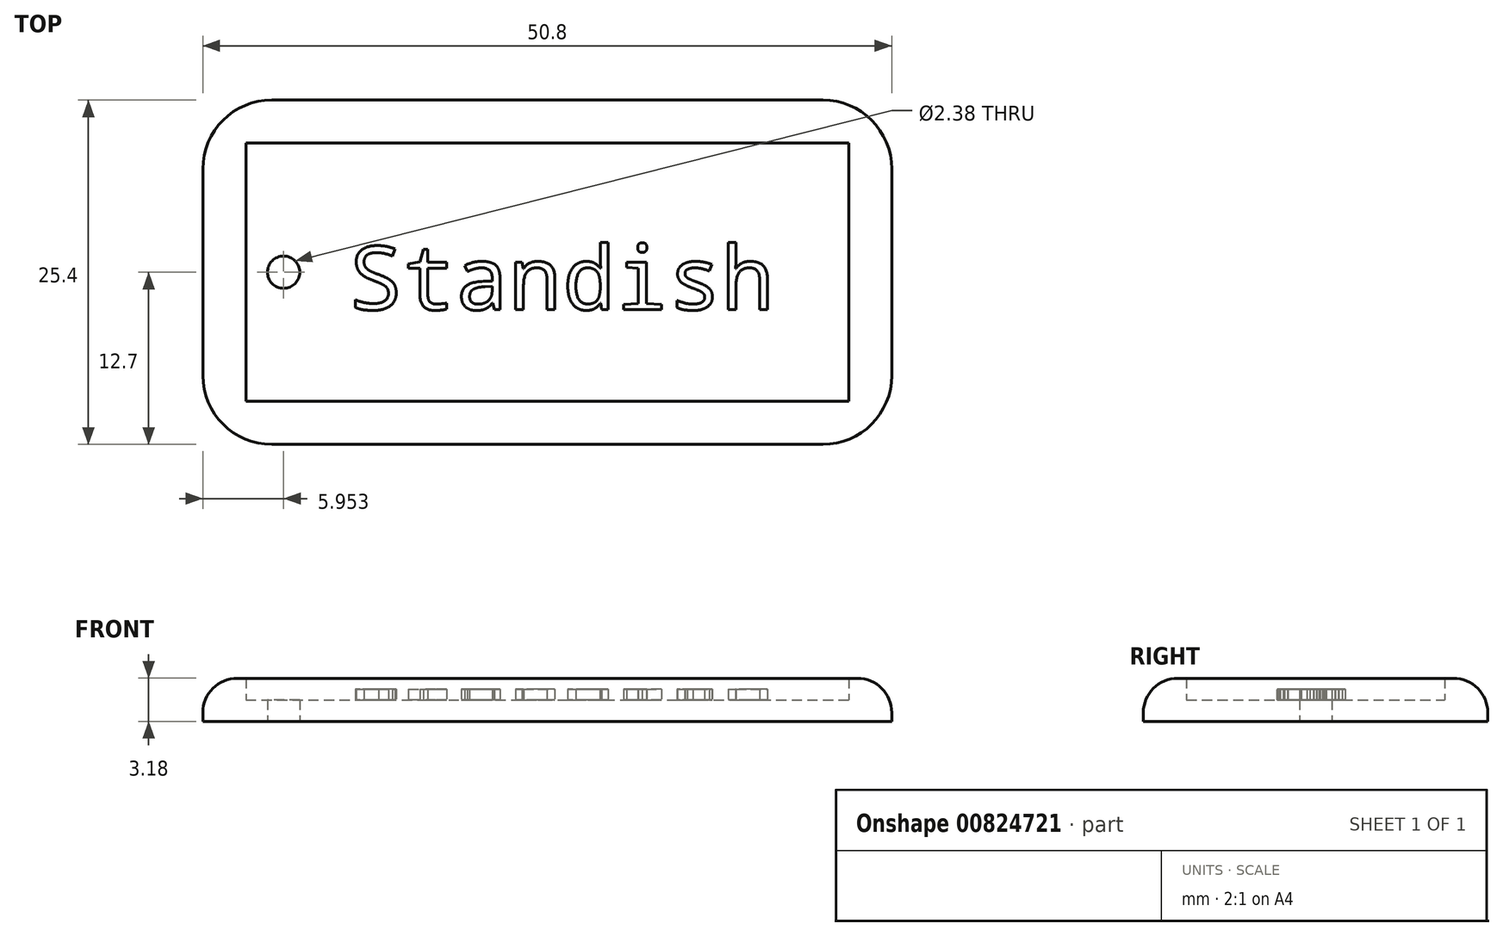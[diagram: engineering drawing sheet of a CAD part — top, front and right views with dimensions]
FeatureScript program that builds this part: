
annotation { "Feature Type Name" : "Feature", "Feature Type Description" : "" }
export const myFeature = defineFeature(function(context is Context, id is Id, definition is map)
    precondition{}
    {
        {
            var Q0;
            Q0=qCreatedBy(makeId("Top.planeOp"),FACE);
            var sketch = newSketch(context, id + "F0", { "sketchPlane" : qUnion([Q0])});
            skLineSegment(sketch, "E0.bottom", {"start": v(0, 0) * mm, "end": v(50.8, 0) * mm});
            skLineSegment(sketch, "E0.top", {"start": v(0, 25.4) * mm, "end": v(50.8, 25.4) * mm});
            skLineSegment(sketch, "E0.left", {"start": v(0, 0) * mm, "end": v(0, 25.4) * mm});
            skLineSegment(sketch, "E0.right", {"start": v(50.8, 0) * mm, "end": v(50.8, 25.4) * mm});
            skCircle(sketch, "E1", {"center": v(5.95, 12.7) * mm, "radius": 1.2 * mm});
            skPoint(sketch, "E1.centerSnap0", {"position": v(0, 12.7) * mm});
            skLineSegment(sketch, "E2.0", {"start": v(3.18, 22.23) * mm, "end": v(47.62, 22.23) * mm});
            skLineSegment(sketch, "E2.1", {"start": v(3.18, 3.18) * mm, "end": v(3.17, 22.23) * mm});
            skLineSegment(sketch, "E2.2", {"start": v(3.18, 3.18) * mm, "end": v(47.62, 3.18) * mm});
            skLineSegment(sketch, "E2.3", {"start": v(47.62, 3.18) * mm, "end": v(47.62, 22.23) * mm});
            skSolve(sketch);
        }
        {
            var Q0;
            Q0=makeQuery(id+"F0.imprint","IMPRINT",FACE,{"disambiguationData":[TD([[makeQuery(id+"F0.imprint","IMPRINT",EDGE,{"derivedFrom":sQuery(id+"F0.wireOp",EDGE,"E1")}),-1.0]])]});
            extrude(context, id + "F1", {"entities" : qUnion([Q0]), "depth" : 1.59 * mm, "offsetDistance" : 25.4 * mm});
        }
        {
            var Q0;
            Q0 = qSketchRegion(id + "F0", true);
            extrude(context, id + "F2", {"entities" : qUnion([Q0]), "operationType" : NewBodyOperationType.ADD, "depth" : 3.17 * mm, "offsetDistance" : 25.4 * mm});
        }
        {
            var Q0;
            Q0=makeQuery(id+"F2.opExtrude","SWEPT_EDGE",EDGE,{"disambiguationData":[OSD([sQuery(id+"F0.wireOp",EDGE,"E0.top"),sQuery(id+"F0.wireOp",EDGE,"E0.right")])]});
            var Q1;
            Q1=makeQuery(id+"F2.opExtrude","SWEPT_EDGE",EDGE,{"disambiguationData":[OSD([sQuery(id+"F0.wireOp",EDGE,"E0.bottom"),sQuery(id+"F0.wireOp",EDGE,"E0.right")])]});
            var Q2;
            Q2=makeQuery(id+"F2.opExtrude","SWEPT_EDGE",EDGE,{"disambiguationData":[OSD([sQuery(id+"F0.wireOp",EDGE,"E0.bottom"),sQuery(id+"F0.wireOp",EDGE,"E0.left")])]});
            var Q3;
            Q3=makeQuery(id+"F2.opExtrude","SWEPT_EDGE",EDGE,{"disambiguationData":[OSD([sQuery(id+"F0.wireOp",EDGE,"E0.top"),sQuery(id+"F0.wireOp",EDGE,"E0.left")])]});
            fillet(context, id + "F3", {"entities" : qUnion([Q0, Q1, Q2, Q3]), "radius" : 5.08 * mm, "tangentPropagation" : true, "allowEdgeOverflow" : false});
        }
        {
            var Q0;
            Q0=makeQuery(id+"F2.opExtrude","CAP_EDGE",EDGE,{"disambiguationData":[OSD([sQuery(id+"F0.wireOp",EDGE,"E0.top")])],"isStart":false});
            fillet(context, id + "F4", {"entities" : qUnion([Q0]), "radius" : 2.54 * mm, "tangentPropagation" : true, "allowEdgeOverflow" : false});
        }
        {
            var Q0;
            Q0=makeQuery(id+"F1.opExtrude","CAP_FACE",FACE,{"disambiguationData":[OSD([sQuery(id+"F0.wireOp",EDGE,"E1"),sQuery(id+"F0.wireOp",EDGE,"E2.0"),sQuery(id+"F0.wireOp",EDGE,"E2.1"),sQuery(id+"F0.wireOp",EDGE,"E2.2"),sQuery(id+"F0.wireOp",EDGE,"E2.3")])],"isStart":false});
            var sketch = newSketch(context, id + "F5", { "sketchPlane" : qUnion([Q0])});
            skText(sketch, "E3", { "text": "Standish\n", "fontName": "DroidSansMono.ttf"});
            const initialGuessF5  = {"E3": [0.0108, 0.00994, 1, 0, 0.0047]};
            skSetInitialGuess(sketch, initialGuessF5);
            skSolve(sketch);
        }
        {
            var Q0;
            Q0 = qSketchRegion(id + "F5", true);
            extrude(context, id + "F6", {"entities" : qUnion([Q0]), "operationType" : NewBodyOperationType.ADD, "depth" : 0.8 * mm, "offsetDistance" : 25.4 * mm});
        }
    });
